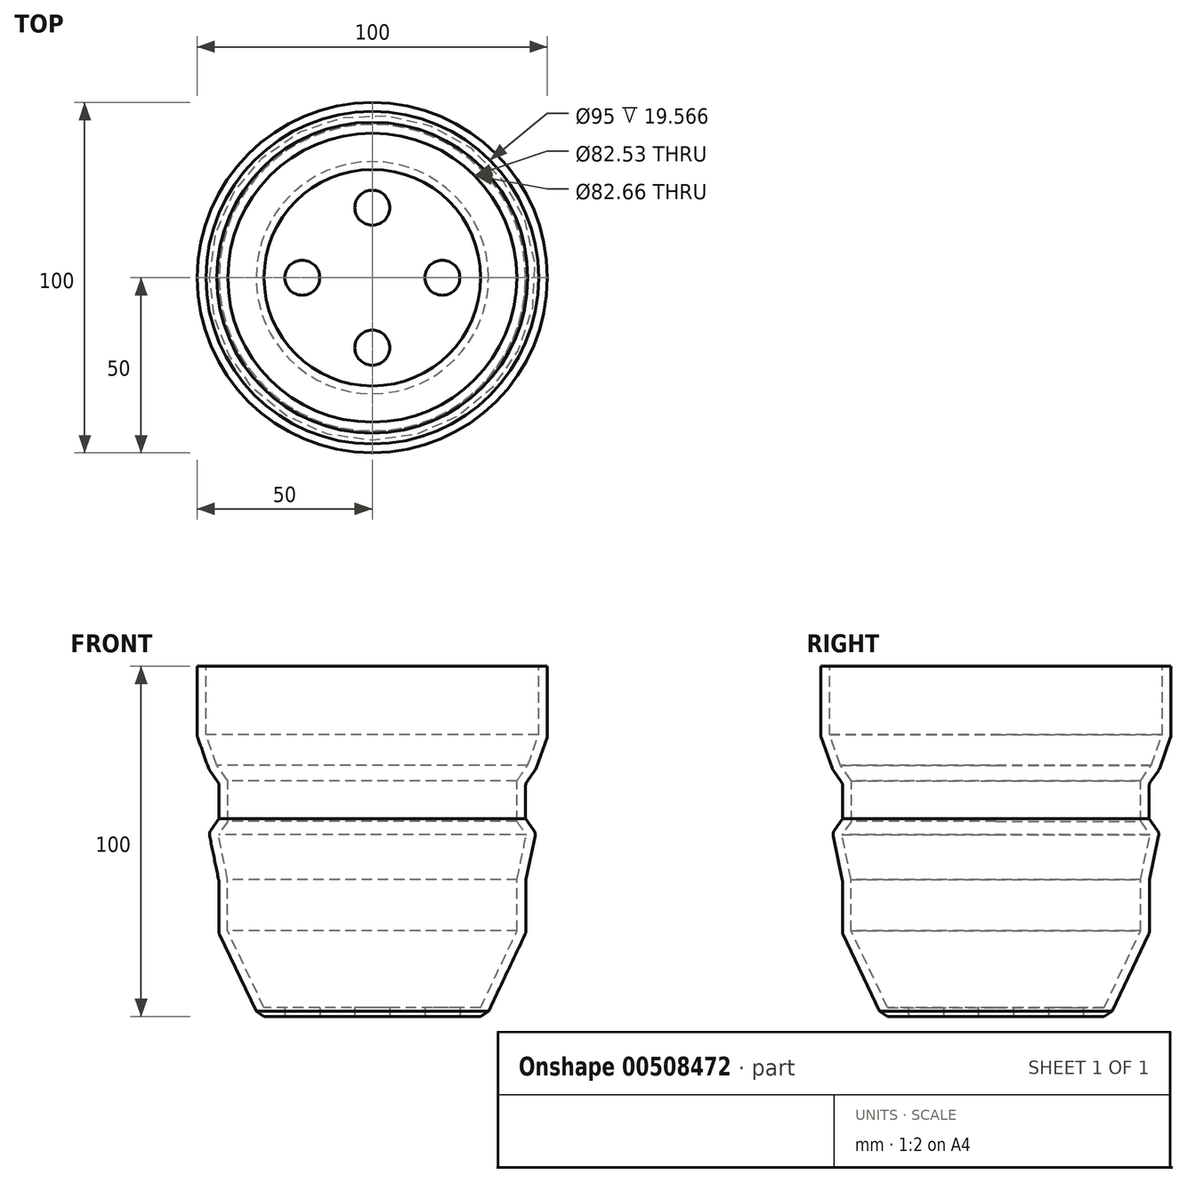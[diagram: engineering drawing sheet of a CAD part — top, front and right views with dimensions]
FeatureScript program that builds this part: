
annotation { "Feature Type Name" : "Feature", "Feature Type Description" : "" }
export const myFeature = defineFeature(function(context is Context, id is Id, definition is map)
    precondition{}
    {
        {
            var Q0;
            Q0=qCreatedBy(makeId("Front.planeOp"),FACE);
            var sketch = newSketch(context, id + "F0", { "sketchPlane" : qUnion([Q0])});
            skLineSegment(sketch, "E0", {"start": v(-50, 80) * mm, "end": v(-46.63, 70.58) * mm});
            skLineSegment(sketch, "E1", {"start": v(0, 0) * mm, "end": v(-32.5, 0) * mm});
            skLineSegment(sketch, "E2", {"start": v(-43.83, 23.86) * mm, "end": v(-32.5, 0) * mm});
            skLineSegment(sketch, "E3", {"start": v(0, 100) * mm, "end": v(0, 0) * mm});
            skLineSegment(sketch, "E4", {"start": v(-50, 100) * mm, "end": v(-50, 80) * mm});
            skLineSegment(sketch, "E5", {"start": v(-50, 100) * mm, "end": v(0, 100) * mm});
            skLineSegment(sketch, "E6", {"start": v(-32.5, 0) * mm, "end": v(-32.5, 40.84) * mm});
            skLineSegment(sketch, "E7", {"start": v(-46.63, 70.58) * mm, "end": v(-43.76, 66.49) * mm});
            skLineSegment(sketch, "E8", {"start": v(-43.76, 66.49) * mm, "end": v(-43.76, 56.49) * mm});
            skLineSegment(sketch, "E9", {"start": v(-43.76, 56.49) * mm, "end": v(-46.63, 52.4) * mm});
            skLineSegment(sketch, "E10", {"start": v(-43.83, 23.86) * mm, "end": v(-43.83, 38.86) * mm});
            skLineSegment(sketch, "E11", {"start": v(-46.63, 52.4) * mm, "end": v(-43.83, 38.86) * mm});
            skSolve(sketch);
        }
        {
            var Q0;
            Q0 = qSketchRegion(id + "F0", true);
            var Q1;
            Q1=sQuery(id+"F0.wireOp",EDGE,"E3");
            revolve(context, id + "F1", {"entities" : qUnion([Q0]), "axis" : qUnion([Q1]), "revolveType" : RevolveType.FULL});
        }
        {
            var Q0;
            Q0=makeQuery(id+"F1.opRevolve","SWEPT_FACE",FACE,{"disambiguationData":[OSD([sQuery(id+"F0.wireOp",EDGE,"E5")])]});
            shell(context, id + "F2", {"entities" : qUnion([Q0]), "thickness" : 2.5 * mm});
        }
        {
            var Q0;
            Q0=makeQuery(id+"F1.opRevolve","SWEPT_EDGE",EDGE,{"disambiguationData":[OSD([sQuery(id+"F0.wireOp",EDGE,"E1"),sQuery(id+"F0.wireOp",EDGE,"E2")])]});
            chamfer(context, id + "F3", {"entities" : qUnion([Q0]), "width" : 2.5 * mm, "tangentPropagation" : true});
        }
        {
            var Q0;
            Q0=makeQuery(id+"F1.opRevolve","SWEPT_FACE",FACE,{"disambiguationData":[OSD([sQuery(id+"F0.wireOp",EDGE,"E1")])]});
            var sketch = newSketch(context, id + "F4", { "sketchPlane" : qUnion([Q0])});
            skCircle(sketch, "E12", {"center": v(0, 20) * mm, "radius": 5 * mm});
            skCircle(sketch, "E13", {"center": v(-20, 0) * mm, "radius": 5 * mm});
            skCircle(sketch, "E14", {"center": v(0, -20) * mm, "radius": 5 * mm});
            skCircle(sketch, "E15", {"center": v(20, 0) * mm, "radius": 5 * mm});
            skSolve(sketch);
        }
        {
            var Q0;
            Q0=makeQuery(id+"F4.imprint","IMPRINT",FACE,{"disambiguationData":[TD([[makeQuery(id+"F4.imprint","IMPRINT",EDGE,{"derivedFrom":sQuery(id+"F4.wireOp",EDGE,"E13")}),1.0]])]});
            var Q1;
            Q1=makeQuery(id+"F4.imprint","IMPRINT",FACE,{"disambiguationData":[TD([[makeQuery(id+"F4.imprint","IMPRINT",EDGE,{"derivedFrom":sQuery(id+"F4.wireOp",EDGE,"E12")}),1.0]])]});
            var Q2;
            Q2=makeQuery(id+"F4.imprint","IMPRINT",FACE,{"disambiguationData":[TD([[makeQuery(id+"F4.imprint","IMPRINT",EDGE,{"derivedFrom":sQuery(id+"F4.wireOp",EDGE,"E15")}),1.0]])]});
            var Q3;
            Q3=makeQuery(id+"F4.imprint","IMPRINT",FACE,{"disambiguationData":[TD([[makeQuery(id+"F4.imprint","IMPRINT",EDGE,{"derivedFrom":sQuery(id+"F4.wireOp",EDGE,"E14")}),1.0]])]});
            extrude(context, id + "F5", {"entities" : qUnion([Q0, Q1, Q2, Q3]), "operationType" : NewBodyOperationType.REMOVE, "oppositeDirection" : true, "depth" : 10 * mm});
        }
        {
            var Q0;
            Q0=makeQuery(id+"F1.opRevolve","SWEPT_EDGE",EDGE,{"disambiguationData":[OSD([sQuery(id+"F0.wireOp",EDGE,"E9"),sQuery(id+"F0.wireOp",EDGE,"E11")])]});
            fillet(context, id + "F6", {"entities" : qUnion([Q0]), "radius" : 2 * mm, "tangentPropagation" : true, "allowEdgeOverflow" : false});
        }
        {
            var Q0;
            Q0=makeQuery(id+"F1.opRevolve","SWEPT_EDGE",EDGE,{"disambiguationData":[OSD([sQuery(id+"F0.wireOp",EDGE,"E2"),sQuery(id+"F0.wireOp",EDGE,"E10")])]});
            var Q1;
            Q1=makeQuery(id+"F1.opRevolve","SWEPT_EDGE",EDGE,{"disambiguationData":[OSD([sQuery(id+"F0.wireOp",EDGE,"E0"),sQuery(id+"F0.wireOp",EDGE,"E4")])]});
            var Q2;
            Q2=makeQuery(id+"F1.opRevolve","SWEPT_EDGE",EDGE,{"disambiguationData":[OSD([sQuery(id+"F0.wireOp",EDGE,"E10"),sQuery(id+"F0.wireOp",EDGE,"E11")])]});
            var Q3;
            Q3=makeQuery(id+"F1.opRevolve","SWEPT_EDGE",EDGE,{"disambiguationData":[OSD([sQuery(id+"F0.wireOp",EDGE,"E7"),sQuery(id+"F0.wireOp",EDGE,"E8")])]});
            var Q4;
            Q4=makeQuery(id+"F1.opRevolve","SWEPT_EDGE",EDGE,{"disambiguationData":[OSD([sQuery(id+"F0.wireOp",EDGE,"E0"),sQuery(id+"F0.wireOp",EDGE,"E7")])]});
            fillet(context, id + "F7", {"entities" : qUnion([Q0, Q1, Q2, Q3, Q4]), "radius" : 2 * mm, "tangentPropagation" : true, "allowEdgeOverflow" : false});
        }
    });
